# Revit family: Generator_Diesel
name_source: partatom
category: Electrical Equipment
units: mm (PartAtom-declared; Revit-internal decimal feet)

## family parameters
Always vertical = Yes
Cut with Voids When Loaded = No
OmniClass Number = 23.80.10.11.14.14
OmniClass Title = Electricity Generation Units
Part Type = Other Panel
Room Calculation Point = No
Round Connector Dimension = Use Radius
Shared = No
Work Plane-Based = No

## types (3) — shared parameters
Apparent Load Phase A = 0 VA
Apparent Load Phase B = 0 VA
Apparent Load Phase C = 0 VA
Bus Voltage = 600 V
Coolant Heater Voltage = 480 V
Coolant Heater Voltage Selection = 480 V
Coolant Heater Voltage is 208 V = No
Coolant Heater Voltage is 240 V = No
Coolant Heater Voltage is 480 V = Yes
Coolant Heater Wattage = 4990 W
Coolant Heater is 40 Deg F Ambient = Yes
Coolant Heater is Sub 40 Deg F Ambient = No
Cooling Coil Air Pressure Drop = 0.50 in-wg
Engine Lube Oil Capacity = 27.0 gal
Engine Model = QSK23-G7 NR2
Exhaust System Backpressure = 40.80 in-wg
Frequency = 60 Hz
Fuel Consumption Rate at Full Load = 0.000 gal/h
Load Classification = Power
Number of Poles = 3
Product Material = Steel - Cummins - Green
Voltage = 600
Voltage is 190 = No
Voltage is 200 = No
Voltage is 208 = No
Voltage is 220 = No
Voltage is 240 = No
Voltage is 380 = No
Voltage is 400 = No
Voltage is 416 = No
Voltage is 440 = No
Voltage is 480 = No
Voltage is 600 = Yes
z Engine Length = 74.66 "
z Length to Front of Engine = 70.74 "

## per-type parameters (varying)
| type | Amperage | Description | Emissions CO (g/hp-hr) | Emissions HC (g/hp-hr) | Emissions NOx (g/hp-hr) | Emissions PM (g/hp-hr) | Exhaust Gas Flow Rate | Exhaust Octave Band - 1000 Hz | Exhaust Octave Band - 125 Hz | Exhaust Octave Band - 2000 Hz | Exhaust Octave Band - 250 Hz | Exhaust Octave Band - 4000 Hz | Exhaust Octave Band - 500 Hz | Exhaust Octave Band - 63 Hz | Exhaust Octave Band - 8000 Hz | Exhaust Stack Gas Temp | Heat Rejection to Aftercooler Circuit Coolant | Heat Rejection to Jacket Water Coolant | Manufacturer | Model | Power Rating | URL | Wattage | z Type |
| DQCA - 600 kW Standby Power | 0.722 kA | 600 kW STANDBY Diesel Generator Set | 0.16 | 0.19 | 4.4 | 0.04 | 4830 CFM | 121 | 112.4 | 123.4 | 121.5 | 120.8 | 119.3 | 102.5 | 120 | 824 °F | 635460.0 Btu/h | 864600.0 Btu/h | Cummins Power Generation, Inc. | DQCA | 600.000 kW | http://www.cumminspower.com | 600 | 1 |
| DQCB - 750 kW Standby Power | 0.902 kA | 750 kW STANDBY Diesel Generator Set | 0.22 | 0.13 | 5.9 | 0.05 | 5358 CFM | 124.1 | 113.8 | 124.7 | 123.1 | 123 | 121.6 | 103.9 | 121.4 | 888 °F | 779100.0 Btu/h | 1060140.0 Btu/h | Cummins Power Generation, Inc. | DQCB | 750.000 kW | http://www.cumminspower.com | 750 | 2 |
| DQCC - 800 kW Standby Power | 0.962 kA |  | 0.24 | 0.12 | 6.1 | 0.05 | 5455 CFM | 124.6 | 114 | 125 | 123.5 | 123.4 | 122.2 | 104.1 | 121.5 | 902 °F | 808020.0 Btu/h | 1099500.0 Btu/h |  |  | 800.000 kW |  | 800 | 3 |

## geometry (parser evidence)
native form markers: Blend x18, Sweep x3
no freeform markers — native parametric forms only
